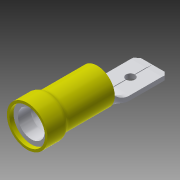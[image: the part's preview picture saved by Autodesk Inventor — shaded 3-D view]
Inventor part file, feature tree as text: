
AUTODESK INVENTOR PART (.ipt)
format: ipt  version: 2014 (Build 180170000, 170)  size: 372,224 bytes
history: native  units: in
note: dims shown in document units (in); Inventor stores cm internally (conversion verified against a paired STEP export)
features: sketch x8, extrude x6, projected_geometry x6, chamfer x4, fillet x2, shell x1, revolve x1, plane x1, loft x1, other x1
ambient origin geometry x8: Origin, YZ Plane, XZ Plane, XY Plane, X Axis, Y Axis, Z Axis, Center Point
bodies: Solid1 (feature_tree), Solid2 (feature_tree)
feature tree (31):
  extrude  "Extrusion1"  Depth=0.5595in TaperAngle=0.0deg
  extrude  "Extrusion2"  Depth=0.157in TaperAngle=0.0deg
  fillet  "Fillet1"  Radius=0.05in
  shell  "Shell1"  Thickness=0.02in
  revolve  "Revolution1"  [1 undecoded]
  plane  "Work Plane1"
  extrude  "Extrusion3"  [1 undecoded]
  loft  "Loft1"
  fillet  "Fillet3"  Radius=0.005in
  chamfer  "Chamfer1"  Distance=0.036in
  extrude  "Extrusion4"  Depth=0.443in
  chamfer  "Chamfer2"  Angle=90.0deg  [1 undecoded]
  chamfer  "Chamfer3"  Distance=0.3937in Angle=90.0deg
  chamfer  "Chamfer4"  Distance=0.005in Angle=45.0deg
  extrude  "Extrusion5"  Depth=0.005in TaperAngle=45.0deg
  extrude  "Extrusion6"  Depth=0.03in TaperAngle=45.0deg
  sketch  "Sketch1"  dims[d0=0.2785in d1=0.5595in d2=0.0in]
  sketch  "Sketch2"  dims[d3=0.324in d4=0.157in d5=0.0in d6=0.05in d7=0.02in]
  projected_geometry  "Projected Loop1"
  sketch  "Sketch3"  dims[d9=0.035in d10=0.035in]
  sketch  "Sketch4"  dims[d11=90.0deg d12=-0.108in]
  sketch  "Sketch5"  dims[d17=0.036in d18=0.0in d24=0.04in]
  projected_geometry  "Projected Loop2"
  sketch  "Sketch6"  dims[d27=0.003in d28=0.125in d29=45.0deg d30=0.005in d31=0.036in d32=0.0in]
  other  "Edges2"
  sketch  "Sketch7"  dims[d33=0.248in d34=0.443in]
  projected_geometry  "Projected Loop3"
  sketch  "Sketch8"  dims[d35=0.1365in d36=0.0in d37=90.0deg d38=0.3937in d39=90.0deg d40=0.05in d41=0.005in d42=45.0deg d43=0.005in d44=0.05in d45=45.0deg d46=0.03in d47=0.05in d48=45.0deg d49=0.0715in d50=1.0in d51=0.0in d52=0.005in d53=0.005in d54=0.0in]
  projected_geometry  "Projected Loop4"
  projected_geometry  "Project Cut Edges1"
  projected_geometry  "Project Cut Edges2"
note: 3 required parameter values undecoded (feature->parameter linkage not recoverable at this tier; creation-order binding heuristic only, values carry confidence <= 0.55)